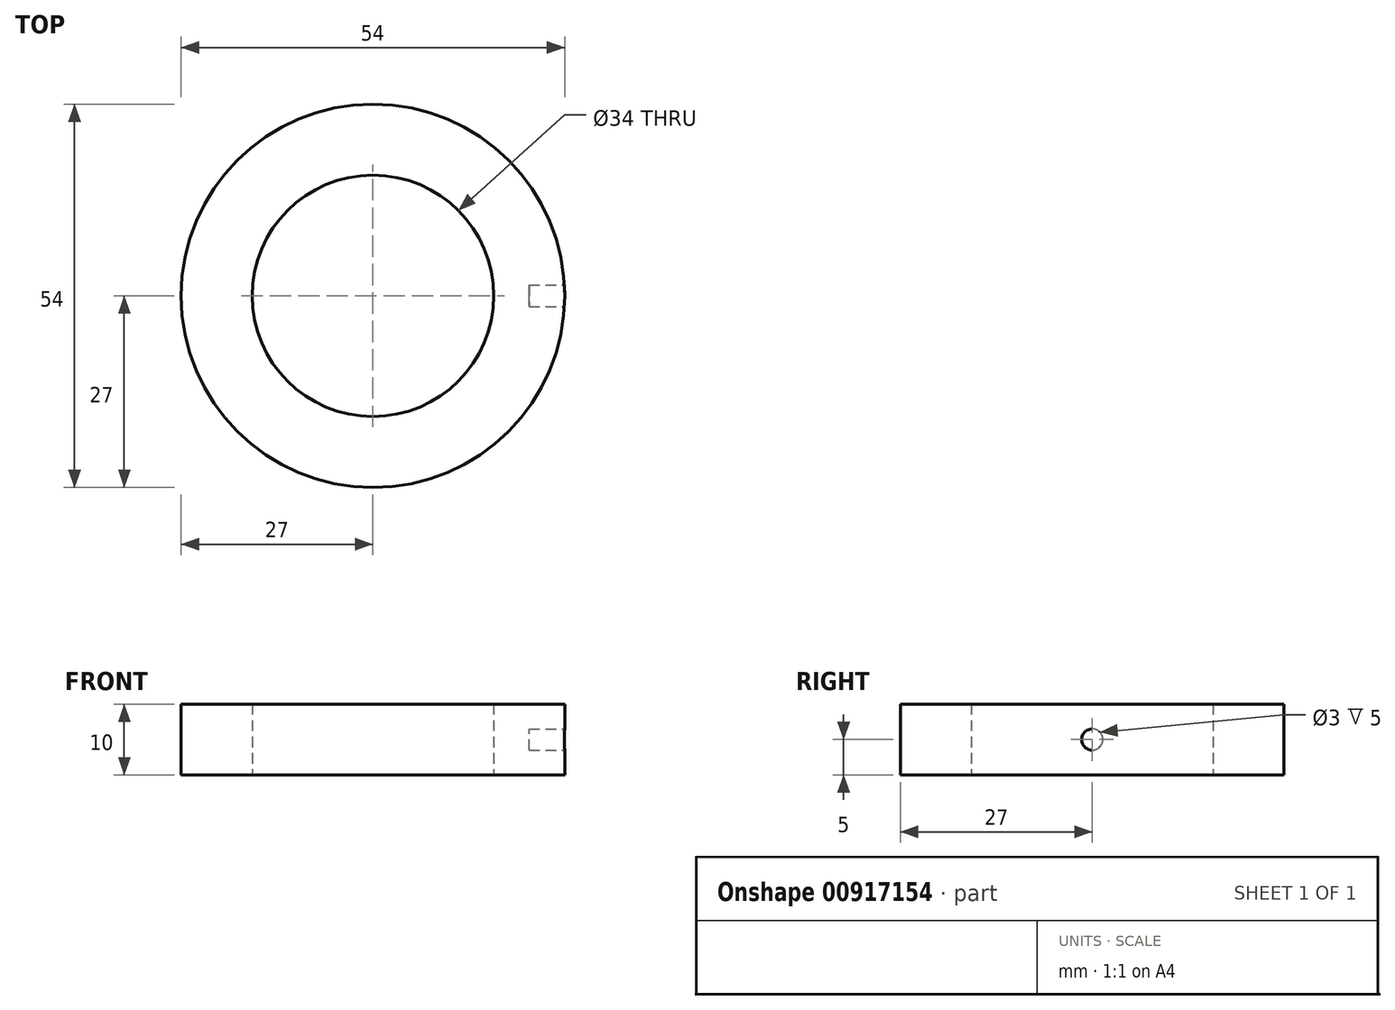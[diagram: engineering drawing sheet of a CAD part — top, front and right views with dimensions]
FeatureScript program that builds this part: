
annotation { "Feature Type Name" : "Feature", "Feature Type Description" : "" }
export const myFeature = defineFeature(function(context is Context, id is Id, definition is map)
    precondition{}
    {
        {
            var Q0;
            Q0=qCreatedBy(makeId("Top.planeOp"),FACE);
            var sketch = newSketch(context, id + "F0", { "sketchPlane" : qUnion([Q0])});
            skCircle(sketch, "E0", {"center": v(0, 0) * mm, "radius": 27 * mm});
            skCircle(sketch, "E1", {"center": v(0, 0) * mm, "radius": 17 * mm});
            skSolve(sketch);
        }
        {
            var Q0;
            Q0 = qSketchRegion(id + "F0", true);
            extrude(context, id + "F1", {"entities" : qUnion([Q0]), "depth" : 10 * mm, "offsetDistance" : 25 * mm});
        }
        {
            var Q0;
            Q0=qCreatedBy(makeId("Right.planeOp"),FACE);
            cPlane(context, id + "F2", {"entities" : qUnion([Q0]), "cplaneType" : CPlaneType.OFFSET, "offset" : 27 * mm, "width" : 150 * mm, "height" : 150 * mm});
        }
        {
            var Q0;
            Q0=qCreatedBy(id+"F2.planeOp",FACE);
            var sketch = newSketch(context, id + "F3", { "sketchPlane" : qUnion([Q0])});
            skCircle(sketch, "E2", {"center": v(0, 5) * mm, "radius": 1.5 * mm});
            skSolve(sketch);
        }
        {
            var Q0;
            Q0 = qSketchRegion(id + "F3", true);
            extrude(context, id + "F4", {"entities" : qUnion([Q0]), "operationType" : NewBodyOperationType.REMOVE, "oppositeDirection" : true, "depth" : 5 * mm, "offsetDistance" : 25 * mm});
        }
    });
